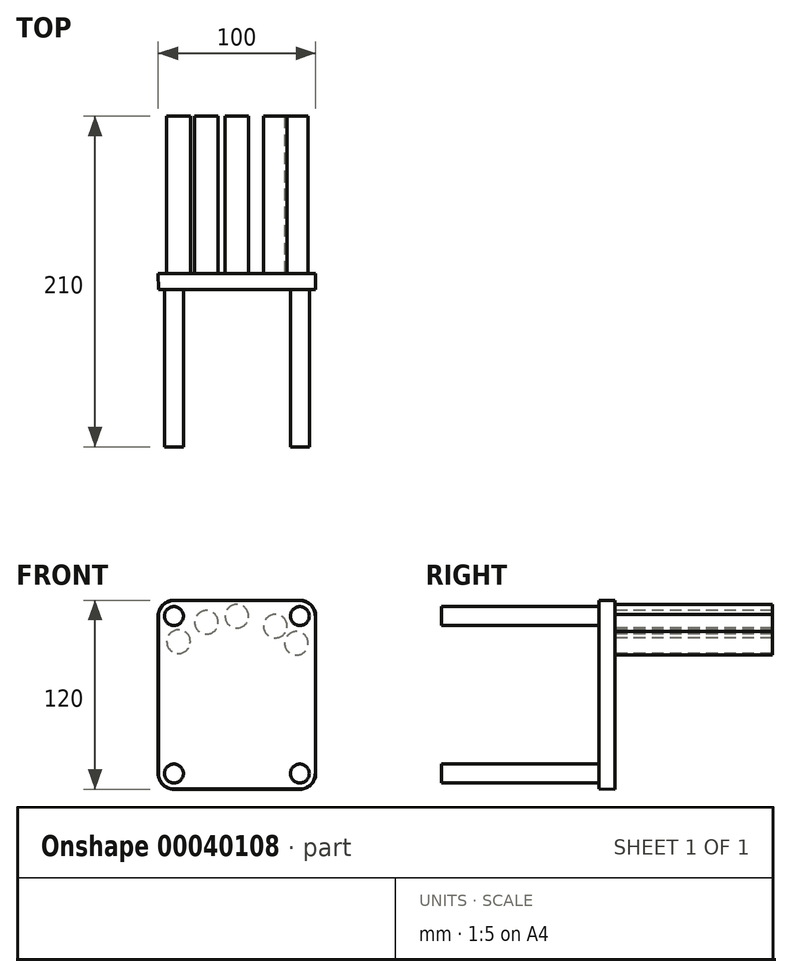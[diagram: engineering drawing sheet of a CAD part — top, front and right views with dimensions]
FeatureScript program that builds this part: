
annotation { "Feature Type Name" : "Feature", "Feature Type Description" : "" }
export const myFeature = defineFeature(function(context is Context, id is Id, definition is map)
    precondition{}
    {
        {
            var Q0;
            Q0=qCreatedBy(makeId("Front.planeOp"),FACE);
            var sketch = newSketch(context, id + "F0", { "sketchPlane" : qUnion([Q0])});
            skLineSegment(sketch, "E0.rect.bottom", {"start": v(40, 60) * mm, "end": v(-40, 60) * mm});
            skLineSegment(sketch, "E0.rect.top", {"start": v(40, -60) * mm, "end": v(-40, -60) * mm});
            skLineSegment(sketch, "E0.rect.left", {"start": v(50, 50) * mm, "end": v(50, -50) * mm});
            skLineSegment(sketch, "E0.rect.right", {"start": v(-50, 50) * mm, "end": v(-50, -50) * mm});
            skPoint(sketch, "E0.rect.middle", {"position": v(0, 0) * mm});
            skPoint(sketch, "E1.visualSharp", {"position": v(-50, 60) * mm});
            skArc(sketch, "E1.filletArc", {"start": v(-40, 60) * mm, "mid": v(-47.07, 57.07) * mm, "end": v(-50, 50) * mm});
            skPoint(sketch, "E2.visualSharp", {"position": v(50, 60) * mm});
            skArc(sketch, "E2.filletArc", {"start": v(50, 50) * mm, "mid": v(47.07, 57.07) * mm, "end": v(40, 60) * mm});
            skPoint(sketch, "E3.visualSharp", {"position": v(50, -60) * mm});
            skArc(sketch, "E3.filletArc", {"start": v(40, -60) * mm, "mid": v(47.07, -57.07) * mm, "end": v(50, -50) * mm});
            skPoint(sketch, "E4.visualSharp", {"position": v(-50, -60) * mm});
            skArc(sketch, "E4.filletArc", {"start": v(-50, -50) * mm, "mid": v(-47.07, -57.07) * mm, "end": v(-40, -60) * mm});
            skSolve(sketch);
        }
        {
            var Q0;
            Q0 = qSketchRegion(id + "F0", true);
            extrude(context, id + "F1", {"entities" : qUnion([Q0]), "depth" : 10 * mm, "hasDraft" : true, "draftAngle" : 1 * degree, "draftPullDirection" : true});
        }
        {
            var Q0;
            Q0=makeQuery(id+"F1.opExtrude","CAP_FACE",FACE,{"disambiguationData":[OSD([sQuery(id+"F0.wireOp",EDGE,"E0.rect.bottom"),sQuery(id+"F0.wireOp",EDGE,"E0.rect.top"),sQuery(id+"F0.wireOp",EDGE,"E0.rect.left"),sQuery(id+"F0.wireOp",EDGE,"E0.rect.right"),sQuery(id+"F0.wireOp",EDGE,"E1.filletArc"),sQuery(id+"F0.wireOp",EDGE,"E2.filletArc"),sQuery(id+"F0.wireOp",EDGE,"E3.filletArc"),sQuery(id+"F0.wireOp",EDGE,"E4.filletArc")])],"isStart":false});
            var sketch = newSketch(context, id + "F2", { "sketchPlane" : qUnion([Q0])});
            skLineSegment(sketch, "E5.bottom", {"start": v(-40, 50) * mm, "end": v(40, 50) * mm, "construction": true});
            skLineSegment(sketch, "E5.top", {"start": v(-40, -50) * mm, "end": v(40, -50) * mm, "construction": true});
            skLineSegment(sketch, "E5.left", {"start": v(-40, 50) * mm, "end": v(-40, -50) * mm, "construction": true});
            skLineSegment(sketch, "E5.right", {"start": v(40, 50) * mm, "end": v(40, -50) * mm, "construction": true});
            skCircle(sketch, "E6", {"center": v(-40, 50) * mm, "radius": 6 * mm});
            skCircle(sketch, "E7", {"center": v(40, 50) * mm, "radius": 6 * mm});
            skCircle(sketch, "E8", {"center": v(40, -50) * mm, "radius": 6 * mm});
            skCircle(sketch, "E9", {"center": v(-40, -50) * mm, "radius": 6 * mm});
            skSolve(sketch);
        }
        {
            var Q0;
            Q0=makeQuery(id+"F2.imprint","IMPRINT",FACE,{"disambiguationData":[TD([[makeQuery(id+"F2.imprint","IMPRINT",EDGE,{"derivedFrom":sQuery(id+"F2.wireOp",EDGE,"E6")}),1.0]])]});
            var Q1;
            Q1=makeQuery(id+"F2.imprint","IMPRINT",FACE,{"disambiguationData":[TD([[makeQuery(id+"F2.imprint","IMPRINT",EDGE,{"derivedFrom":sQuery(id+"F2.wireOp",EDGE,"E7")}),1.0]])]});
            var Q2;
            Q2=makeQuery(id+"F2.imprint","IMPRINT",FACE,{"disambiguationData":[TD([[makeQuery(id+"F2.imprint","IMPRINT",EDGE,{"derivedFrom":sQuery(id+"F2.wireOp",EDGE,"E8")}),1.0]])]});
            var Q3;
            Q3=makeQuery(id+"F2.imprint","IMPRINT",FACE,{"disambiguationData":[TD([[makeQuery(id+"F2.imprint","IMPRINT",EDGE,{"derivedFrom":sQuery(id+"F2.wireOp",EDGE,"E9")}),1.0]])]});
            extrude(context, id + "F3", {"entities" : qUnion([Q0, Q1, Q2, Q3]), "operationType" : NewBodyOperationType.ADD, "depth" : 100 * mm});
        }
        {
            var Q0;
            Q0=makeQuery(id+"F1.opExtrude","CAP_FACE",FACE,{"disambiguationData":[OSD([sQuery(id+"F0.wireOp",EDGE,"E0.rect.bottom"),sQuery(id+"F0.wireOp",EDGE,"E0.rect.top"),sQuery(id+"F0.wireOp",EDGE,"E0.rect.left"),sQuery(id+"F0.wireOp",EDGE,"E0.rect.right"),sQuery(id+"F0.wireOp",EDGE,"E1.filletArc"),sQuery(id+"F0.wireOp",EDGE,"E2.filletArc"),sQuery(id+"F0.wireOp",EDGE,"E3.filletArc"),sQuery(id+"F0.wireOp",EDGE,"E4.filletArc")])],"isStart":true});
            var sketch = newSketch(context, id + "F4", { "sketchPlane" : qUnion([Q0])});
            skArc(sketch, "E10", {"start": v(36.97, 33.66) * mm, "mid": v(-0.64, 50) * mm, "end": v(-37.82, 32.7) * mm, "construction": true});
            skCircle(sketch, "E11", {"center": v(-37.82, 32.7) * mm, "radius": 7.5 * mm});
            skCircle(sketch, "E12", {"center": v(-24.41, 43.63) * mm, "radius": 7.5 * mm});
            skCircle(sketch, "E13", {"center": v(0, 49.89) * mm, "radius": 7.5 * mm});
            skCircle(sketch, "E14", {"center": v(19.32, 46.02) * mm, "radius": 7.5 * mm});
            skCircle(sketch, "E15", {"center": v(37.05, 33.75) * mm, "radius": 7.5 * mm});
            skSolve(sketch);
        }
        {
            var Q0;
            Q0 = qSketchRegion(id + "F4", true);
            extrude(context, id + "F5", {"entities" : qUnion([Q0]), "operationType" : NewBodyOperationType.ADD, "depth" : 100 * mm});
        }
    });
